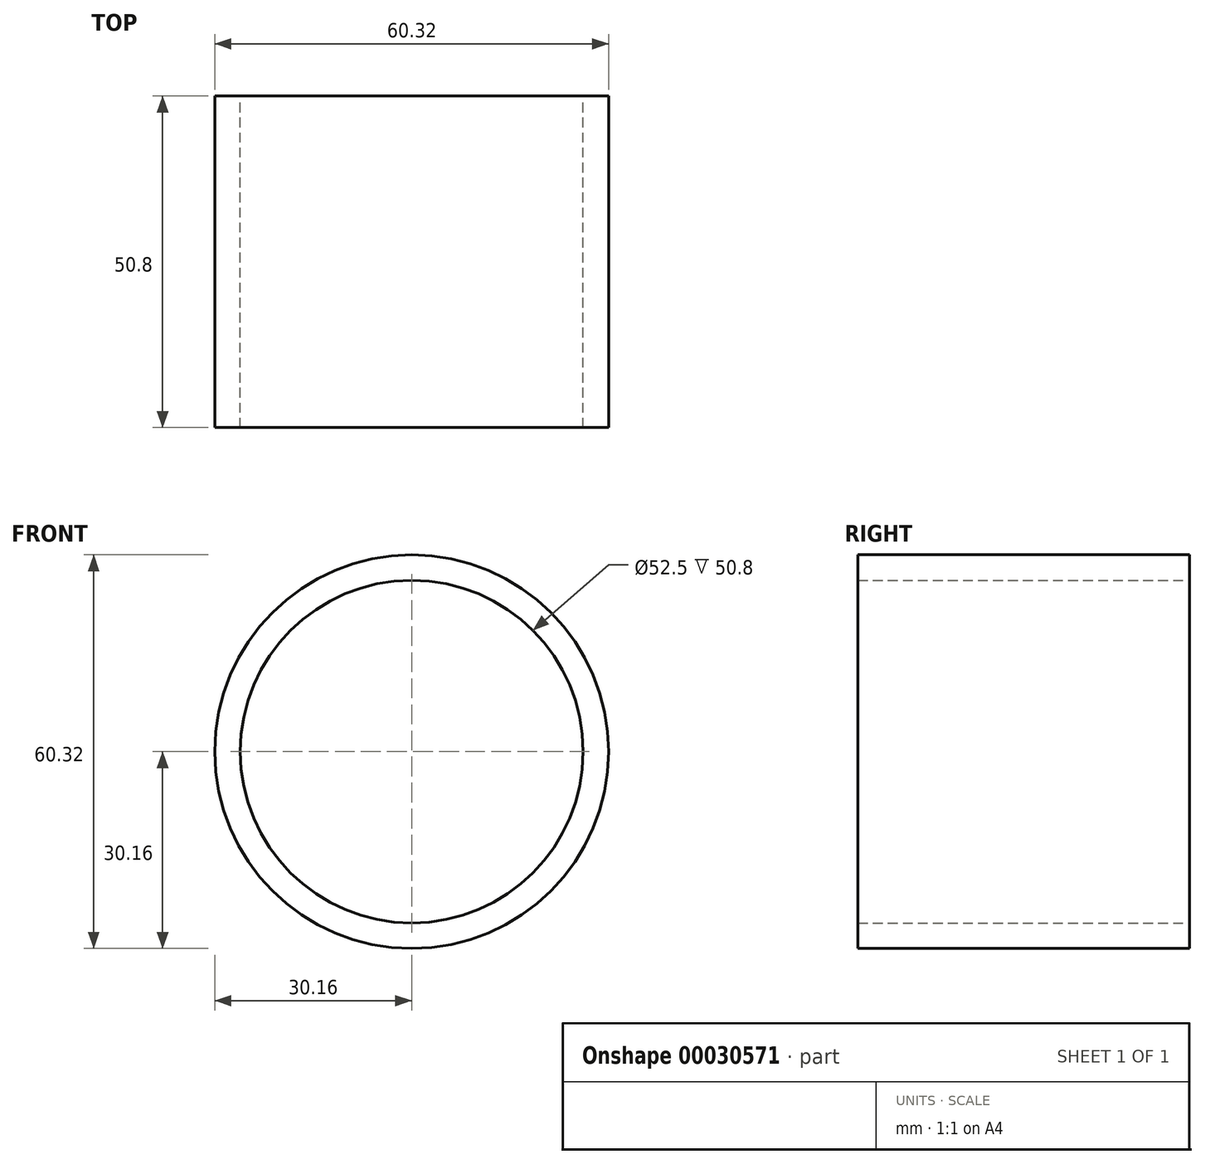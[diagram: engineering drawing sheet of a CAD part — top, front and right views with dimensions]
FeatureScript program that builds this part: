
annotation { "Feature Type Name" : "Feature", "Feature Type Description" : "" }
export const myFeature = defineFeature(function(context is Context, id is Id, definition is map)
    precondition{}
    {
        {
            var Q0;
            Q0=qCreatedBy(makeId("Front.planeOp"),FACE);
            var sketch = newSketch(context, id + "F0", { "sketchPlane" : qUnion([Q0])});
            skCircle(sketch, "E0", {"center": v(0, 0) * mm, "radius": 30.16 * mm});
            skCircle(sketch, "E1.0", {"center": v(0, 0) * mm, "radius": 26.25 * mm});
            skSolve(sketch);
        }
        {
            var Q0;
            Q0=makeQuery(id+"F0.imprint","IMPRINT",FACE,{"disambiguationData":[TD([[makeQuery(id+"F0.imprint","IMPRINT",EDGE,{"derivedFrom":sQuery(id+"F0.wireOp",EDGE,"E0")}),1.0]])]});
            extrude(context, id + "F1", {"entities" : qUnion([Q0]), "endBound" : BoundingType.SYMMETRIC, "depth" : 50.8 * mm});
        }
    });
